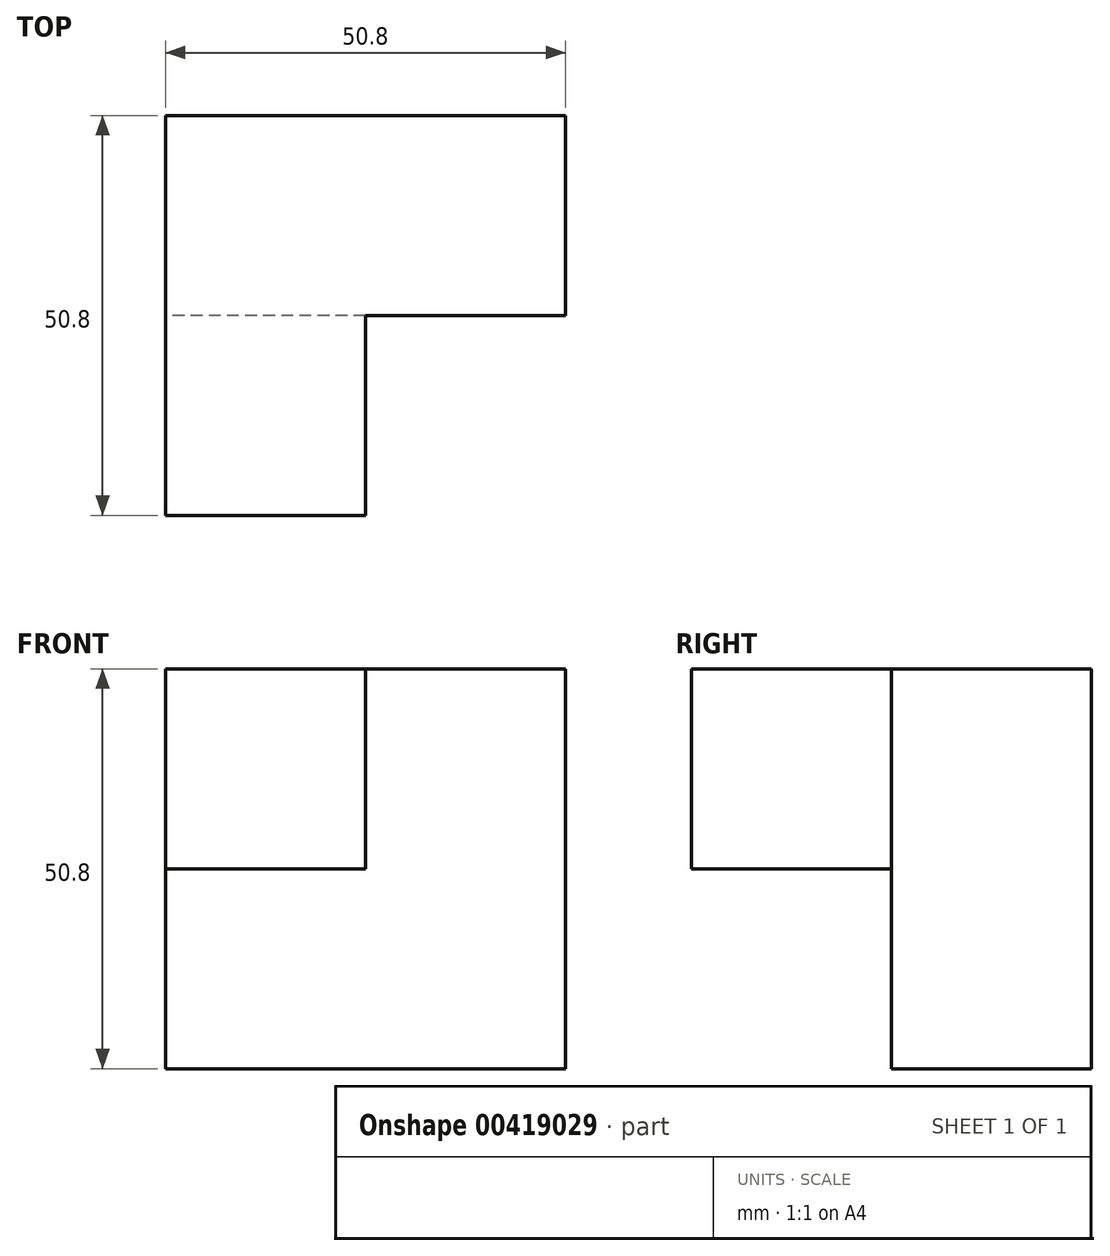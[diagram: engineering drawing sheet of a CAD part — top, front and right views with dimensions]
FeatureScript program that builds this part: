
annotation { "Feature Type Name" : "Feature", "Feature Type Description" : "" }
export const myFeature = defineFeature(function(context is Context, id is Id, definition is map)
    precondition{}
    {
        {
            var Q0;
            Q0=qCreatedBy(makeId("Front.planeOp"),FACE);
            var sketch = newSketch(context, id + "F0", { "sketchPlane" : qUnion([Q0])});
            skLineSegment(sketch, "E0", {"start": v(0, 0) * mm, "end": v(0, 50.8) * mm});
            skLineSegment(sketch, "E1", {"start": v(0, 50.8) * mm, "end": v(-50.8, 50.8) * mm});
            skLineSegment(sketch, "E2", {"start": v(-50.8, 50.8) * mm, "end": v(-50.8, 0) * mm});
            skLineSegment(sketch, "E3", {"start": v(-50.8, 0) * mm, "end": v(0, 0) * mm});
            skSolve(sketch);
        }
        {
            var Q0;
            Q0=makeQuery(id+"F0.imprint","IMPRINT",FACE,{"disambiguationData":[TD([[makeQuery(id+"F0.imprint","IMPRINT",EDGE,{"derivedFrom":sQuery(id+"F0.wireOp",EDGE,"E0")}),1.0]])]});
            extrude(context, id + "F1", {"entities" : qUnion([Q0]), "depth" : 25.4 * mm});
        }
        {
            var Q0;
            Q0=makeQuery(id+"F1.opExtrude","CAP_FACE",FACE,{"disambiguationData":[OSD([sQuery(id+"F0.wireOp",EDGE,"E0"),sQuery(id+"F0.wireOp",EDGE,"E1"),sQuery(id+"F0.wireOp",EDGE,"E2"),sQuery(id+"F0.wireOp",EDGE,"E3")])],"isStart":false});
            var sketch = newSketch(context, id + "F2", { "sketchPlane" : qUnion([Q0])});
            skLineSegment(sketch, "E4", {"start": v(-25.4, 50.8) * mm, "end": v(-25.4, 25.4) * mm});
            skLineSegment(sketch, "E5", {"start": v(-25.4, 25.4) * mm, "end": v(-50.8, 25.4) * mm});
            skSolve(sketch);
        }
        {
            var Q0;
            Q0 = qSketchRegion(id + "F2", true);
            var Q1;
            {var subQ0=sQuery(id+"F2.wireOp",EDGE,"E4");Q1=makeQuery(id+"F2.imprint","IMPRINT",FACE,{"disambiguationData":[TD([[makeQuery(id+"F2.imprint","IMPRINT",EDGE,{"derivedFrom":subQ0}),-1.0]])]});}
            extrude(context, id + "F3", {"entities" : qUnion([Q0, Q1]), "operationType" : NewBodyOperationType.ADD, "depth" : 25.4 * mm});
        }
    });
